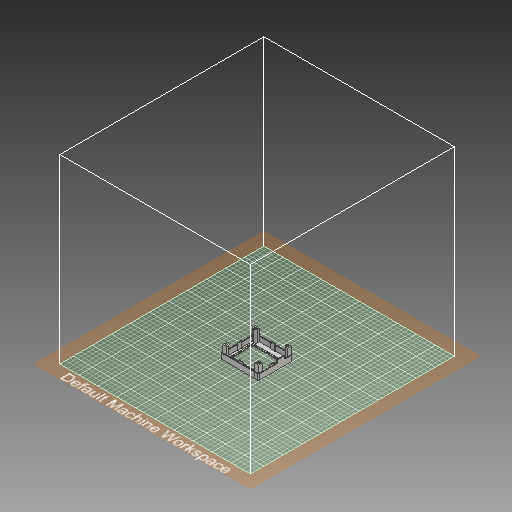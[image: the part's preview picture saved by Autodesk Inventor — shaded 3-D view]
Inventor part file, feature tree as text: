
AUTODESK INVENTOR PART (.ipt)
format: ipt  version: 2019 (Build 230136000, 136)  size: 660,480 bytes
history: native  units: mm
features: other x9, extrude x9, sketch x3, hole x1, fillet x1, projected_geometry x1
ambient origin geometry x8: Origin, YZ Plane, XZ Plane, XY Plane, X Axis, Y Axis, Z Axis, Center Point
bodies: Solid1 (feature_tree)
feature tree (24):
  other  "case_top"
  extrude  "Extrusion1"  Depth=72.0mm
  extrude  "Extrusion2"  Depth=7.0mm
  other  "resetTL_zarez_vedeni"
  extrude  "Extrusion3"  Depth=64.2mm
  extrude  "Extrusion4"  Depth=5.8mm
  extrude  "Extrusion7"  Depth=1.5mm
  hole  "Hole1"  [1 undecoded]
  extrude  "Extrusion8"  Depth=1.5mm
  extrude  "Extrusion9"  Depth=23.15mm
  extrude  "Extrusion10"  Depth=0.8mm
  fillet  "Fillet1"  Radius=3.0mm
  extrude  "Extrusion11"  Depth=4.5mm
  other  "vrsek"
  other  "displej_vyrez"
  other  "resetTL_vnitrek_vybrani"
  other  "resetTL_dira"
  other  "spojeni_srouby"
  other  "diry_zavitova_vlozka"
  sketch  "Sketch10"  dims[d0=78.5mm d1=72.0mm]
  projected_geometry  "Projected Loop1"
  other  "dira_RJ45"
  sketch  "Sketch12"  dims[d2=1.2mm d3=0.0mm d4=7.0mm]
  sketch  "Sketch13"  dims[d5=23.15mm d6=64.2mm d7=5.8mm d8=1.5mm d9=12.4mm d10=1.5mm d11=23.15mm d12=36.0mm d13=3.0mm d14=0.0mm d15=4.5mm d16=7.0mm d19=2.0mm d20=21.0mm d21=0.9mm d22=0.0mm d23=3.0mm d24=2.0mm d25=0.0mm d45=8.0mm d47=26.5mm d48=0.0mm d49=3.3mm d50=6.0mm d51=3.75mm d52=2.0mm d53=1.745329mm d54=12.0mm d55=0.0mm d56=0.4mm d57=0.0mm d58=2.5mm d59=0.4mm d60=0.0mm d61=1.6mm d62=16.8mm d64=0.0mm d65=17.3mm d66=1.6mm d67=0.0mm d68=0.0mm d70=10.5mm d71=1.6mm d72=0.0mm d73=0.0mm d74=15.45mm d75=2.0mm d76=1.2mm d77=10.0mm d79=0.0mm d80=0.8mm d81=0.4mm d82=10.0mm d83=1.2mm d84=0.0mm d86=0.0mm d87=0.8mm d89=10.0mm d90=1.2mm d91=0.0mm d92=0.0mm d93=1.2mm d94=10.0mm d95=0.0mm d96=0.0mm d97=0.8mm d98=14.0mm d99=1.0mm d100=0.0mm d101=0.0mm d106=31.15mm d107=4.2mm d108=7.0mm d109=0.8mm]
note: 1 required parameter value undecoded (feature->parameter linkage not recoverable at this tier; creation-order binding heuristic only, values carry confidence <= 0.55)
